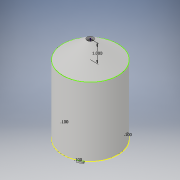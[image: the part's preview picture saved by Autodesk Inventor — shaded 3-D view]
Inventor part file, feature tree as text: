
AUTODESK INVENTOR PART (.ipt)
format: ipt  version: 2017 (Build 210142000, 142)  size: 236,032 bytes
history: native  units: in
note: dims shown in document units (in); Inventor stores cm internally (conversion verified against a paired STEP export)
features: extrude x11, sketch x5, plane x1, revolve x1
ambient origin geometry x8: Origin, YZ Plane, XZ Plane, XY Plane, X Axis, Y Axis, Z Axis, Center Point
bodies: Solid1 (feature_tree), Solid2 (feature_tree)
feature tree (18):
  extrude  "Extrusion1"  Depth=0.96in
  sketch  "Sketch2"  dims[d10=0.96in d13=3.8in d14=0.0in]
  sketch  "3D Sketch1"
  plane  "Work Plane3"
  revolve  "Revolution1"  [1 undecoded]
  sketch  "Sketch5"  dims[d18=90.0deg d20=2.84in d26=2.92in d31=0.125in d32=0.0in d33=0.1in d34=0.1in d35=0.1in d36=0.125in d37=0.0in d38=0.125in d39=0.0in d40=0.0625in d41=0.0in d42=0.0625in d43=0.0in d44=0.0625in d45=0.0in d46=0.0625in d47=0.0in d48=0.0625in d49=0.0in d50=0.0625in d51=0.0in d52=0.0625in d53=0.0in]
  extrude  "Extrusion2"  Depth=0.175in
  extrude  "Extrusion3"  Depth=0.0625in
  extrude  "Extrusion4"  Depth=0.0625in
  extrude  "Extrusion5"  Depth=0.125in TaperAngle=0.0deg
  extrude  "Extrusion6"  Depth=0.0625in
  extrude  "Extrusion7"  Depth=0.0625in
  extrude  "Extrusion8"  Depth=0.0625in
  extrude  "Extrusion9"  Depth=0.125in TaperAngle=0.0deg
  extrude  "Extrusion10"  Depth=0.125in TaperAngle=0.0deg
  extrude  "Extrusion11"  Depth=0.0625in TaperAngle=0.0deg
  sketch  "Sketch1"  dims[d0=0.96in d6=0.96in]
  sketch  "Sketch4"  dims[d15=1.0in d17=0.175in]
note: 1 required parameter value undecoded (feature->parameter linkage not recoverable at this tier; creation-order binding heuristic only, values carry confidence <= 0.55)
